# Revit family: Spout-American_Standard-Tub Spout-888811X
name_source: partatom
category: Plumbing Fixtures
revit_build: Autodesk Revit 2018 (Build: 20170223_1515(x64)
units: mm (PartAtom-declared; Revit-internal decimal feet)

## family parameters
Cut with Voids When Loaded = No
Host = Face
OmniClass Number = 23.45.05.14.17
OmniClass Title = Showers
Part Type = Normal
Room Calculation Point = No
Round Connector Dimension = Use Diameter
Shared = Yes

## types (4) — shared parameters
Assembly Code = D2020300
CW Connection = Yes
CWFU = 3
Default Elevation = 21"
Finish = Metal-American_Standard-002-Polished_Chrome
HW Connection = Yes
HWFU = 3
Height = 2 5/8"
Installation Type = Wall Mounted
Length = 7 5/16"
Manufacturer = American Standard
Material = Metal-American Standard-002-Polished_Chrome
Price = Prices may vary. Please consult Manufacturer Representative for most up-to-date price list.
Product Documentation Link = https://www.americanstandard-us.com
Product Page URL = https://www.americanstandard-us.com
Revised Date = 04/28/2021
Type Comments = Town Square S Slip-On Non-Diverter Tub Spout
URL = https://www.americanstandard-us.com
Vent Connection = No
Warranty Information = Limited Lifetime Function and Finish Warranty
Waste Connection = No
Water Connection Diameter = 1/2"
Water Connection Radius = 1/4"
Width = 2 5/8"
zero-valued in all types: WFU

## per-type parameters (varying)
| type | Connection Description | Description | Pull-Up Handle |
| 8888110 | 1/2" Slip-On Supply Inlet | Slip-On Non-Diverter Tub Spout | No |
| 8888111 | 1/2" IPS Supply Inlet | Non-Diverter 1/2" IPS Tub Spout | No |
| 8888108 | 1/2" IPS Supply Inlet | Diverter 1/2" IPS Tub Spout | Yes |
| 8888109 | 1/2" IPS Supply Inlet | Slip-On Diverter Tub Spout | Yes |

note: column(s) folded — value = type name in every type: Model

## geometry (parser evidence)
native form markers: Sweep x3
no freeform markers — native parametric forms only
